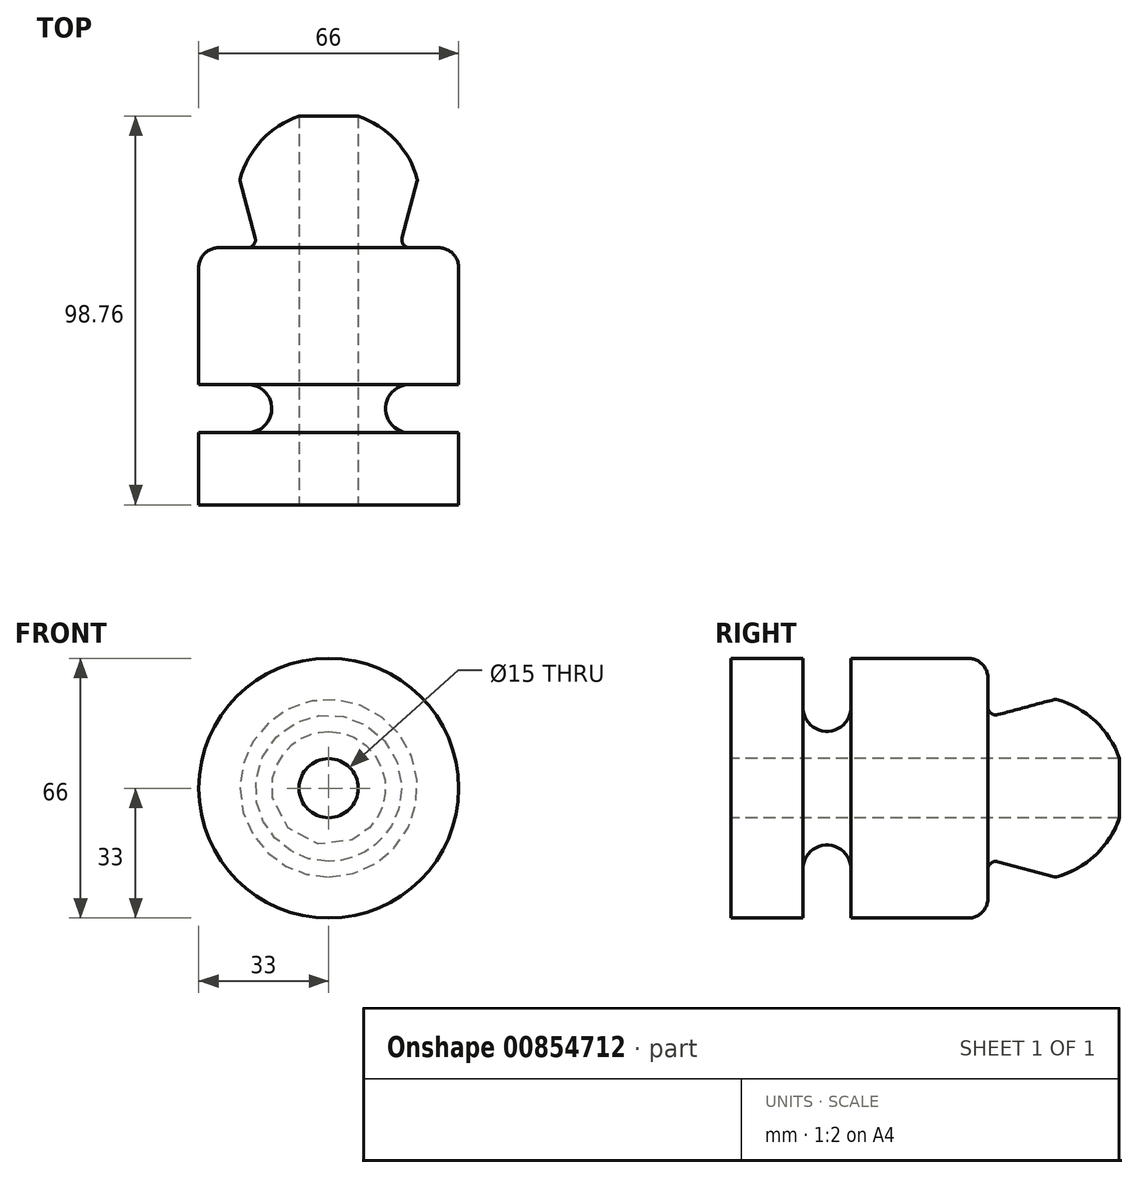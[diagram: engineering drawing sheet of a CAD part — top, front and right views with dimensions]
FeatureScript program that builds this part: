
annotation { "Feature Type Name" : "Feature", "Feature Type Description" : "" }
export const myFeature = defineFeature(function(context is Context, id is Id, definition is map)
    precondition{}
    {
        {
            var Q0;
            Q0=qCreatedBy(makeId("Top.planeOp"),FACE);
            var sketch = newSketch(context, id + "F0", { "sketchPlane" : qUnion([Q0])});
            skLineSegment(sketch, "E0", {"start": v(0, 100) * mm, "end": v(0, 0) * mm, "construction": true});
            skLineSegment(sketch, "E1", {"start": v(0, 0) * mm, "end": v(33, 0) * mm});
            skLineSegment(sketch, "E2", {"start": v(33, 0) * mm, "end": v(33, 18.32) * mm});
            skLineSegment(sketch, "E3", {"start": v(33, 18.32) * mm, "end": v(20.56, 18.32) * mm});
            skLineSegment(sketch, "E4", {"start": v(20.56, 30.56) * mm, "end": v(33, 30.56) * mm});
            skLineSegment(sketch, "E5", {"start": v(33, 30.56) * mm, "end": v(33, 65.32) * mm});
            skLineSegment(sketch, "E6", {"start": v(33, 65.32) * mm, "end": v(18, 65.32) * mm});
            skLineSegment(sketch, "E7", {"start": v(18, 65.32) * mm, "end": v(22.59, 82.45) * mm});
            skLineSegment(sketch, "E8", {"start": v(0, 100) * mm, "end": v(0, 0) * mm});
            skArc(sketch, "E9", {"start": v(22.59, 82.45) * mm, "mid": v(14.3, 95.1) * mm, "end": v(0, 100) * mm});
            skArc(sketch, "E10", {"start": v(20.56, 30.56) * mm, "mid": v(14.44, 24.44) * mm, "end": v(20.56, 18.32) * mm});
            skSolve(sketch);
        }
        {
            var Q0;
            Q0=makeQuery(id+"F0.imprint","IMPRINT",FACE,{"disambiguationData":[TD([[makeQuery(id+"F0.imprint","IMPRINT",EDGE,{"derivedFrom":sQuery(id+"F0.wireOp",EDGE,"E1")}),1.0]])]});
            var Q1;
            Q1=sQuery(id+"F0.wireOp",EDGE,"E8");
            revolve(context, id + "F1", {"surfaceOperationType" : NewSurfaceOperationType.NEW, "entities" : qUnion([Q0]), "axis" : qUnion([Q1]), "revolveType" : RevolveType.FULL});
        }
        {
            var Q0;
            Q0=makeQuery(id+"F1.opRevolve","SWEPT_EDGE",EDGE,{"disambiguationData":[OSD([sQuery(id+"F0.wireOp",EDGE,"E5"),sQuery(id+"F0.wireOp",EDGE,"E6")])]});
            fillet(context, id + "F2", {"entities" : qUnion([Q0]), "radius" : 5 * mm, "tangentPropagation" : true, "allowEdgeOverflow" : false});
        }
        {
            var Q0;
            Q0=makeQuery(id+"F1.opRevolve","SWEPT_EDGE",EDGE,{"disambiguationData":[OSD([sQuery(id+"F0.wireOp",EDGE,"E6"),sQuery(id+"F0.wireOp",EDGE,"E7")])]});
            fillet(context, id + "F3", {"entities" : qUnion([Q0]), "radius" : 2 * mm, "tangentPropagation" : true, "allowEdgeOverflow" : false});
        }
        {
            var Q0;
            Q0=makeQuery(id+"F1.opRevolve","SWEPT_FACE",FACE,{"disambiguationData":[OSD([sQuery(id+"F0.wireOp",EDGE,"E1")])]});
            var sketch = newSketch(context, id + "F4", { "sketchPlane" : qUnion([Q0])});
            skCircle(sketch, "E11", {"center": v(0, 0) * mm, "radius": 7.5 * mm});
            skSolve(sketch);
        }
        {
            var Q0;
            Q0 = qSketchRegion(id + "F4", true);
            extrude(context, id + "F5", {"entities" : qUnion([Q0]), "operationType" : NewBodyOperationType.REMOVE, "oppositeDirection" : true, "depth" : 120 * mm, "offsetDistance" : 25 * mm});
        }
        {
            var Q0;
            Q0=makeQuery(id+"F1.opRevolve","SWEPT_EDGE",EDGE,{"disambiguationData":[OSD([sQuery(id+"F0.wireOp",EDGE,"E7"),sQuery(id+"F0.wireOp",EDGE,"E9")])]});
            fillet(context, id + "F6", {"entities" : qUnion([Q0]), "radius" : 1 * mm, "tangentPropagation" : true, "allowEdgeOverflow" : false});
        }
    });
